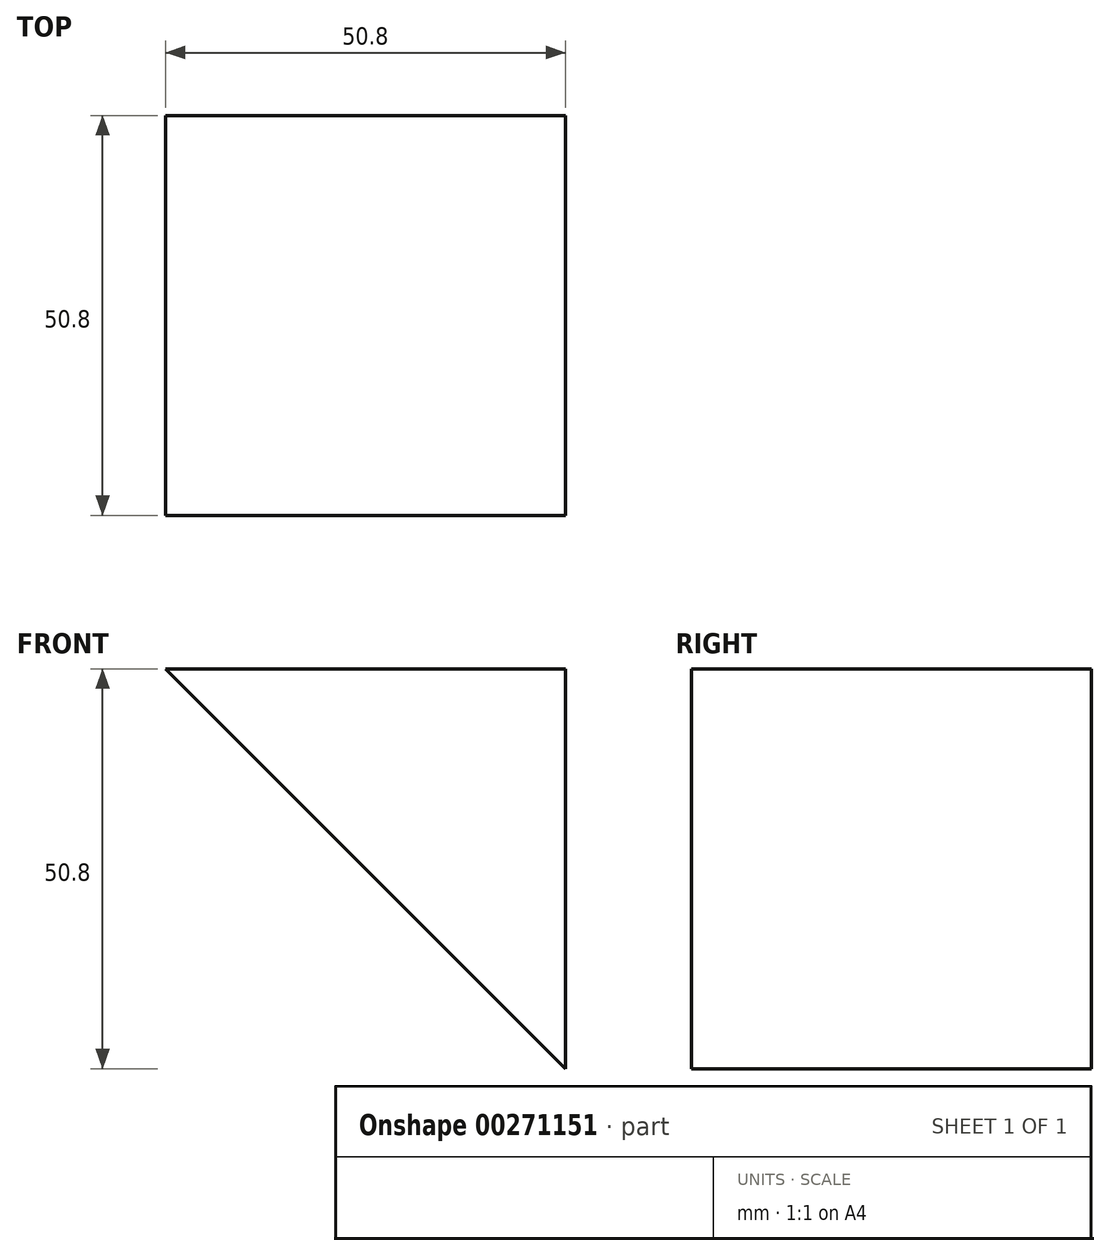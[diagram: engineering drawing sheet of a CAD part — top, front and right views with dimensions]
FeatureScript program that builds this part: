
annotation { "Feature Type Name" : "Feature", "Feature Type Description" : "" }
export const myFeature = defineFeature(function(context is Context, id is Id, definition is map)
    precondition{}
    {
        {
            var Q0;
            Q0=qCreatedBy(makeId("Front.planeOp"),FACE);
            var sketch = newSketch(context, id + "F0", { "sketchPlane" : qUnion([Q0])});
            skLineSegment(sketch, "E0", {"start": v(0, 0) * mm, "end": v(0, 50.8) * mm});
            skLineSegment(sketch, "E1", {"start": v(0, 50.8) * mm, "end": v(-50.8, 50.8) * mm});
            skLineSegment(sketch, "E2", {"start": v(-50.8, 50.8) * mm, "end": v(0, 0) * mm});
            skSolve(sketch);
        }
        {
            var Q0;
            Q0 = qSketchRegion(id + "F0", true);
            extrude(context, id + "F1", {"entities" : qUnion([Q0]), "depth" : 50.8 * mm});
        }
    });
